# Revit family: 122
name_source: partatom
category: Pipe Accessories
revit_build: Autodesk Revit 2018 (Build: 20170223_1515(x64)
units: mm (PartAtom-declared; Revit-internal decimal feet)

## family parameters
Always vertical = Yes
Cut with Voids When Loaded = No
OmniClass Number = 23.27.43.00
OmniClass Title = Pipe Fittings
Part Type = Valve - Breaks Into
Round Connector Dimension = Use Diameter
Shared = No
Work Plane-Based = No

## types (3) — shared parameters
Assembly Code = D2040100
BIMobject category = Valves
Description = Butterfly valve + screws + nuts + washers
Design country = Italy
Edition number = 1
F = 265 mm
IFC Classification = Pipe Fitting
Keynote = 15410
Lookup Table Name = Butterfly Valve + Screws + Nuts + Washers - 90710
Manufacturer = Aignep Spa
Manufacturer country = Italy
Manufacturer name = Aignep Spa
Material main = Aluminium
Model = 90710
OmniClass Code = 23-27 43 00
OmniClass Description = Pipe Fittings
Product Guid = b4a93527-2693-4edf-bdb3-f11859421d76
Product Material = AIGNEP - Steel - Blue
Product SKU = Butterfly-Valve-Screws-Nuts-Washers-90710
Product certification = https://www.aignep.com
Product data url = https://www.bimobject.com
Product family = INFINITY
Product group = Valves
Product name = Butterfly Valve + Screws + Nuts + Washers - 90710
Product url = https://www.aignep.com
QR code = https://www.bimobject.com
URL = https://www.aignep.com

## per-type parameters (varying)
| type | 110 | 168 | 80 | A | B | C | DN | DO | Diameter Outside | E | Handle Position | Middle Part D | Nominal Diameter |
| D 80 | No | No | Yes | 87 mm | 216 mm | 46 mm | 77 mm | 11.576 mm | 103.152 mm | 160 mm | 146.631 mm  [stored 0.481073 ft] | 107.37 mm | 80.000 mm |
| D 110 | Yes | No | No | 106 mm | 201 mm | 52 mm | 100 mm  [stored 0.328084 ft] | 20 mm  [stored 0.0656168 ft] | 150 mm | 180 mm | 167 mm | 154.218 mm | 110.000 mm |
| D 168 | No | Yes | No | 126 mm  [stored 0.413386 ft] | 202 mm | 56 mm  [stored 0.183727 ft] | 150 mm | 17.106 mm | 202.212 mm  [stored 0.663425 ft] | 240 mm | 192 mm  [stored 0.629921 ft] | 206.43 mm | 168.000 mm |

note: [stored X ft] marks values corroborated as IEEE doubles in the binary element streams (Revit-internal decimal feet)

## geometry (parser evidence)
native form markers: Sweep x5
no freeform markers — native parametric forms only
